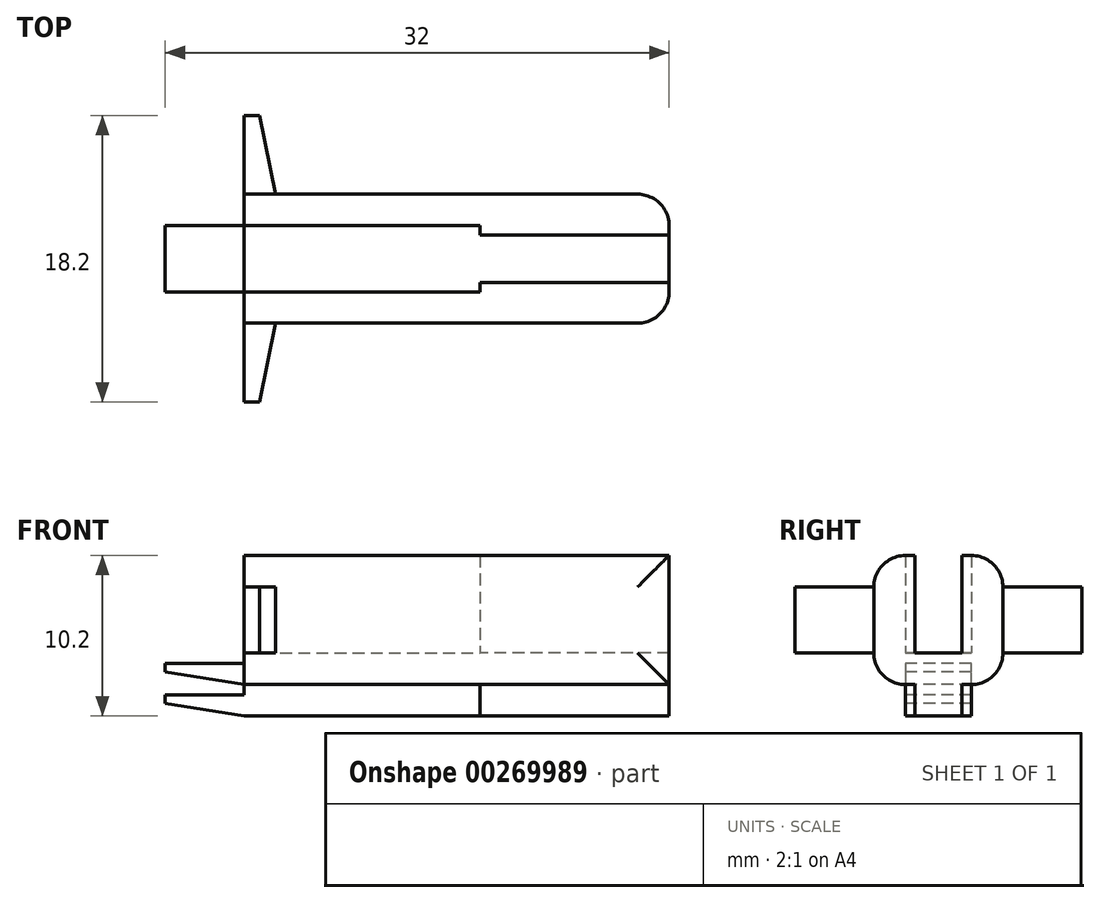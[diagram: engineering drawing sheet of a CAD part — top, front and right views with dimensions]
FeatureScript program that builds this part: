
annotation { "Feature Type Name" : "Feature", "Feature Type Description" : "" }
export const myFeature = defineFeature(function(context is Context, id is Id, definition is map)
    precondition{}
    {
        {
            var Q0;
            Q0=qCreatedBy(makeId("Top.planeOp"),FACE);
            var sketch = newSketch(context, id + "F0", { "sketchPlane" : qUnion([Q0])});
            skLineSegment(sketch, "E0.bottom", {"start": v(7.5, 2.1) * mm, "end": v(-7.5, 2.1) * mm});
            skLineSegment(sketch, "E0.top", {"start": v(7.5, -2.1) * mm, "end": v(-7.5, -2.1) * mm});
            skLineSegment(sketch, "E0.left", {"start": v(7.5, 2.1) * mm, "end": v(7.5, -2.1) * mm});
            skLineSegment(sketch, "E0.right", {"start": v(-7.5, 2.1) * mm, "end": v(-7.5, -2.1) * mm});
            skPoint(sketch, "E0.middle", {"position": v(0, 0) * mm});
            skLineSegment(sketch, "E1.bottom", {"start": v(7.5, 1.5) * mm, "end": v(19.5, 1.5) * mm});
            skLineSegment(sketch, "E1.top", {"start": v(7.5, -1.5) * mm, "end": v(19.5, -1.5) * mm});
            skLineSegment(sketch, "E1.left", {"start": v(7.5, 1.5) * mm, "end": v(7.5, -1.5) * mm});
            skLineSegment(sketch, "E1.right", {"start": v(19.5, 1.5) * mm, "end": v(19.5, -1.5) * mm});
            skPoint(sketch, "E1.middle", {"position": v(13.5, 0) * mm});
            skLineSegment(sketch, "E2", {"start": v(-7.5, 2.1) * mm, "end": v(-7.5, 4.1) * mm});
            skLineSegment(sketch, "E3", {"start": v(-7.5, 4.1) * mm, "end": v(19.5, 4.1) * mm});
            skLineSegment(sketch, "E4", {"start": v(19.5, 4.1) * mm, "end": v(19.5, 1.5) * mm});
            skLineSegment(sketch, "E5.MirrorCS", {"start": v(-7.5, -4.1) * mm, "end": v(19.5, -4.1) * mm});
            skLineSegment(sketch, "E6.MirrorCS", {"start": v(-7.5, -2.1) * mm, "end": v(-7.5, -4.1) * mm});
            skLineSegment(sketch, "E7.MirrorCS", {"start": v(19.5, -4.1) * mm, "end": v(19.5, -1.5) * mm});
            skSolve(sketch);
        }
        {
            var Q0;
            {var subQ3=sQuery(id+"F0.wireOp",EDGE,"E0.bottom");Q0=makeQuery(id+"F0.imprint","IMPRINT",FACE,{"disambiguationData":[TD([[makeQuery(id+"F0.imprint","IMPRINT",EDGE,{"derivedFrom":subQ3}),1.0]])]});}
            var Q1;
            Q1=makeQuery(id+"F0.imprint","IMPRINT",FACE,{"disambiguationData":[TD([[makeQuery(id+"F0.imprint","IMPRINT",EDGE,{"derivedFrom":sQuery(id+"F0.wireOp",EDGE,"E1.bottom")}),-1.0]])]});
            var Q2;
            {var subQ1=sQuery(id+"F0.wireOp",EDGE,"E0.bottom");Q2=makeQuery(id+"F0.imprint","IMPRINT",FACE,{"disambiguationData":[TD([[makeQuery(id+"F0.imprint","IMPRINT",EDGE,{"derivedFrom":subQ1}),-1.0]])]});}
            var Q3;
            {var subQ0=sQuery(id+"F0.wireOp",EDGE,"E0.top");Q3=makeQuery(id+"F0.imprint","IMPRINT",FACE,{"disambiguationData":[TD([[makeQuery(id+"F0.imprint","IMPRINT",EDGE,{"derivedFrom":subQ0}),1.0]])]});}
            extrude(context, id + "F1", {"entities" : qUnion([Q0, Q1, Q2, Q3]), "depth" : 2 * mm, "offsetDistance" : 25 * mm});
        }
        {
            var Q0;
            {var subQ0=sQuery(id+"F0.wireOp",EDGE,"E0.top");Q0=makeQuery(id+"F0.imprint","IMPRINT",FACE,{"disambiguationData":[TD([[makeQuery(id+"F0.imprint","IMPRINT",EDGE,{"derivedFrom":subQ0}),1.0]])]});}
            var Q1;
            {var subQ1=sQuery(id+"F0.wireOp",EDGE,"E0.bottom");Q1=makeQuery(id+"F0.imprint","IMPRINT",FACE,{"disambiguationData":[TD([[makeQuery(id+"F0.imprint","IMPRINT",EDGE,{"derivedFrom":subQ1}),-1.0]])]});}
            extrude(context, id + "F2", {"entities" : qUnion([Q0, Q1]), "operationType" : NewBodyOperationType.ADD, "depth" : 8.2 * mm, "offsetDistance" : 25 * mm});
        }
        {
            var Q0;
            {var subQ0=sQuery(id+"F0.wireOp",EDGE,"E7.MirrorCS");var subQ1=sQuery(id+"F0.wireOp",EDGE,"E5.MirrorCS");Q0=makeQuery(id+"F2.boolean.opBoolean","MERGE",EDGE,{"derivedFrom":[makeQuery(id+"F1.opExtrude","SWEPT_EDGE",EDGE,{"disambiguationData":[OSD([subQ1,subQ0])]}),makeQuery(id+"F2.opExtrude","SWEPT_EDGE",EDGE,{"disambiguationData":[OSD([subQ1,subQ0])]})]});}
            var Q1;
            {var subQ0=sQuery(id+"F0.wireOp",EDGE,"E4");var subQ1=sQuery(id+"F0.wireOp",EDGE,"E3");Q1=makeQuery(id+"F2.boolean.opBoolean","MERGE",EDGE,{"derivedFrom":[makeQuery(id+"F1.opExtrude","SWEPT_EDGE",EDGE,{"disambiguationData":[OSD([subQ1,subQ0])]}),makeQuery(id+"F2.opExtrude","SWEPT_EDGE",EDGE,{"disambiguationData":[OSD([subQ1,subQ0])]})]});}
            var Q2;
            Q2=makeQuery(id+"F2.opExtrude","CAP_EDGE",EDGE,{"disambiguationData":[OSD([sQuery(id+"F0.wireOp",EDGE,"E5.MirrorCS")])],"isStart":false});
            var Q3;
            Q3=makeQuery(id+"F2.opExtrude","CAP_EDGE",EDGE,{"disambiguationData":[OSD([sQuery(id+"F0.wireOp",EDGE,"E3")])],"isStart":false});
            var Q4;
            Q4=makeQuery(id+"F1.opExtrude","CAP_EDGE",EDGE,{"disambiguationData":[OSD([sQuery(id+"F0.wireOp",EDGE,"E3")])],"isStart":true});
            var Q5;
            Q5=makeQuery(id+"F1.opExtrude","CAP_EDGE",EDGE,{"disambiguationData":[OSD([sQuery(id+"F0.wireOp",EDGE,"E5.MirrorCS")])],"isStart":true});
            fillet(context, id + "F3", {"entities" : qUnion([Q0, Q1, Q2, Q3, Q4, Q5]), "tangentPropagation" : true, "radius" : 2 * mm, "defaultsChanged" : false, "vertexSettings" : [], "allowEdgeOverflow" : false});
        }
        {
            var Q0;
            Q0=makeQuery(id+"F0.imprint","IMPRINT",FACE,{"disambiguationData":[TD([[makeQuery(id+"F0.imprint","IMPRINT",EDGE,{"derivedFrom":sQuery(id+"F0.wireOp",EDGE,"E1.bottom")}),-1.0]])]});
            var Q1;
            {var subQ3=sQuery(id+"F0.wireOp",EDGE,"E0.bottom");Q1=makeQuery(id+"F0.imprint","IMPRINT",FACE,{"disambiguationData":[TD([[makeQuery(id+"F0.imprint","IMPRINT",EDGE,{"derivedFrom":subQ3}),1.0]])]});}
            extrude(context, id + "F4", {"entities" : qUnion([Q0, Q1]), "oppositeDirection" : true, "depth" : 2 * mm, "offsetDistance" : 25 * mm});
        }
        {
            var Q0;
            Q0=makeQuery(id+"F4.opExtrude","SWEPT_FACE",FACE,{"disambiguationData":[OSD([sQuery(id+"F0.wireOp",EDGE,"E0.right")])]});
            var sketch = newSketch(context, id + "F5", { "sketchPlane" : qUnion([Q0])});
            skLineSegment(sketch, "E8", {"start": v(-2.1, -0.66) * mm, "end": v(2.1, -0.66) * mm});
            skSolve(sketch);
        }
        {
            var Q0;
            {var subQ0=sQuery(id+"F5.wireOp",EDGE,"E8");Q0=makeQuery(id+"F5.imprint","IMPRINT",FACE,{"disambiguationData":[TD([[makeQuery(id+"F5.imprint","IMPRINT",EDGE,{"derivedFrom":subQ0}),-1.0]])]});}
            extrude(context, id + "F6", {"entities" : qUnion([Q0]), "operationType" : NewBodyOperationType.ADD, "depth" : 5 * mm, "offsetDistance" : 25 * mm});
        }
        {
            var Q0;
            {var subQ0=sQuery(id+"F0.wireOp",EDGE,"E6.MirrorCS");var subQ1=sQuery(id+"F0.wireOp",EDGE,"E2");Q0=makeQuery(id+"F2.boolean.opBoolean","MERGE",FACE,{"derivedFrom":[makeQuery(id+"F1.opExtrude","SWEPT_FACE",FACE,{"disambiguationData":[OSD([sQuery(id+"F0.wireOp",EDGE,"E0.right"),subQ1,subQ0])]}),makeQuery(id+"F2.opExtrude","SWEPT_FACE",FACE,{"disambiguationData":[OSD([subQ1])]}),makeQuery(id+"F2.opExtrude","SWEPT_FACE",FACE,{"disambiguationData":[OSD([subQ0])]})]});}
            var sketch = newSketch(context, id + "F7", { "sketchPlane" : qUnion([Q0])});
            skLineSegment(sketch, "E9", {"start": v(-2.1, 0) * mm, "end": v(-2.1, 1.34) * mm});
            skLineSegment(sketch, "E10", {"start": v(-2.1, 1.34) * mm, "end": v(2.1, 1.34) * mm});
            skLineSegment(sketch, "E11", {"start": v(2.1, 1.34) * mm, "end": v(2.1, 0) * mm});
            skSolve(sketch);
        }
        {
            var Q0;
            Q0=makeQuery(id+"F7.imprint","IMPRINT",FACE,{"disambiguationData":[TD([[makeQuery(id+"F7.imprint","IMPRINT",EDGE,{"derivedFrom":sQuery(id+"F7.wireOp",EDGE,"E9")}),-1.0]])]});
            extrude(context, id + "F8", {"entities" : qUnion([Q0]), "operationType" : NewBodyOperationType.ADD, "depth" : 5 * mm, "offsetDistance" : 25 * mm});
        }
        {
            var Q0;
            Q0=makeQuery(id+"F6.opExtrude","CAP_EDGE",EDGE,{"disambiguationData":[OSD([sQuery(id+"F0.wireOp",EDGE,"E0.right")])],"isStart":false});
            var Q1;
            Q1=makeQuery(id+"F8.opExtrude","CAP_EDGE",EDGE,{"disambiguationData":[OSD([sQuery(id+"F0.wireOp",EDGE,"E0.right"),sQuery(id+"F0.wireOp",EDGE,"E2"),sQuery(id+"F0.wireOp",EDGE,"E6.MirrorCS")])],"isStart":false});
            chamfer(context, id + "F9", {"entities" : qUnion([Q0, Q1]), "chamferType" : ChamferType.TWO_OFFSETS, "width1" : 0.8 * mm, "oppositeDirection" : false, "width2" : 5 * mm, "tangentPropagation" : true});
        }
        {
            var Q0;
            {var subQ0=sQuery(id+"F0.wireOp",EDGE,"E5.MirrorCS");Q0=makeQuery(id+"F2.boolean.opBoolean","MERGE",FACE,{"derivedFrom":[makeQuery(id+"F1.opExtrude","SWEPT_FACE",FACE,{"disambiguationData":[OSD([subQ0])]}),makeQuery(id+"F2.opExtrude","SWEPT_FACE",FACE,{"disambiguationData":[OSD([subQ0])]})]});}
            var sketch = newSketch(context, id + "F10", { "sketchPlane" : qUnion([Q0])});
            skLineSegment(sketch, "E12.bottom", {"start": v(-7.5, 2) * mm, "end": v(-5.5, 2) * mm});
            skLineSegment(sketch, "E12.top", {"start": v(-7.5, 6.2) * mm, "end": v(-5.5, 6.2) * mm});
            skLineSegment(sketch, "E12.left", {"start": v(-7.5, 2) * mm, "end": v(-7.5, 6.2) * mm});
            skLineSegment(sketch, "E12.right", {"start": v(-5.5, 2) * mm, "end": v(-5.5, 6.2) * mm});
            skSolve(sketch);
        }
        {
            var Q0;
            {var subQ0=sQuery(id+"F0.wireOp",EDGE,"E3");Q0=makeQuery(id+"F2.boolean.opBoolean","MERGE",FACE,{"derivedFrom":[makeQuery(id+"F1.opExtrude","SWEPT_FACE",FACE,{"disambiguationData":[OSD([subQ0])]}),makeQuery(id+"F2.opExtrude","SWEPT_FACE",FACE,{"disambiguationData":[OSD([subQ0])]})]});}
            var sketch = newSketch(context, id + "F11", { "sketchPlane" : qUnion([Q0])});
            skLineSegment(sketch, "E13.bottom", {"start": v(7.5, 2) * mm, "end": v(5.5, 2) * mm});
            skLineSegment(sketch, "E13.top", {"start": v(7.5, 6.2) * mm, "end": v(5.5, 6.2) * mm});
            skLineSegment(sketch, "E13.left", {"start": v(7.5, 2) * mm, "end": v(7.5, 6.2) * mm});
            skLineSegment(sketch, "E13.right", {"start": v(5.5, 2) * mm, "end": v(5.5, 6.2) * mm});
            skSolve(sketch);
        }
        {
            var Q0;
            Q0=makeQuery(id+"F11.imprint","IMPRINT",FACE,{"disambiguationData":[TD([[makeQuery(id+"F11.imprint","IMPRINT",EDGE,{"derivedFrom":sQuery(id+"F11.wireOp",EDGE,"E13.bottom")}),1.0]])]});
            extrude(context, id + "F12", {"entities" : qUnion([Q0]), "operationType" : NewBodyOperationType.ADD, "depth" : 5 * mm, "offsetDistance" : 25 * mm});
        }
        {
            var Q0;
            Q0=makeQuery(id+"F10.imprint","IMPRINT",FACE,{"disambiguationData":[TD([[makeQuery(id+"F10.imprint","IMPRINT",EDGE,{"derivedFrom":sQuery(id+"F10.wireOp",EDGE,"E12.bottom")}),1.0]])]});
            extrude(context, id + "F13", {"entities" : qUnion([Q0]), "operationType" : NewBodyOperationType.ADD, "depth" : 5 * mm, "offsetDistance" : 25 * mm});
        }
        {
            var Q0;
            Q0=makeQuery(id+"F13.opExtrude","CAP_EDGE",EDGE,{"disambiguationData":[OSD([sQuery(id+"F10.wireOp",EDGE,"E12.right")])],"isStart":false});
            chamfer(context, id + "F14", {"entities" : qUnion([Q0]), "chamferType" : ChamferType.TWO_OFFSETS, "width1" : 1 * mm, "oppositeDirection" : false, "width2" : 5 * mm, "tangentPropagation" : true});
        }
        {
            var Q0;
            Q0=makeQuery(id+"F12.opExtrude","CAP_EDGE",EDGE,{"disambiguationData":[OSD([sQuery(id+"F11.wireOp",EDGE,"E13.right")])],"isStart":false});
            chamfer(context, id + "F15", {"entities" : qUnion([Q0]), "chamferType" : ChamferType.TWO_OFFSETS, "width1" : 5 * mm, "oppositeDirection" : false, "width2" : 1 * mm, "tangentPropagation" : true});
        }
    });
